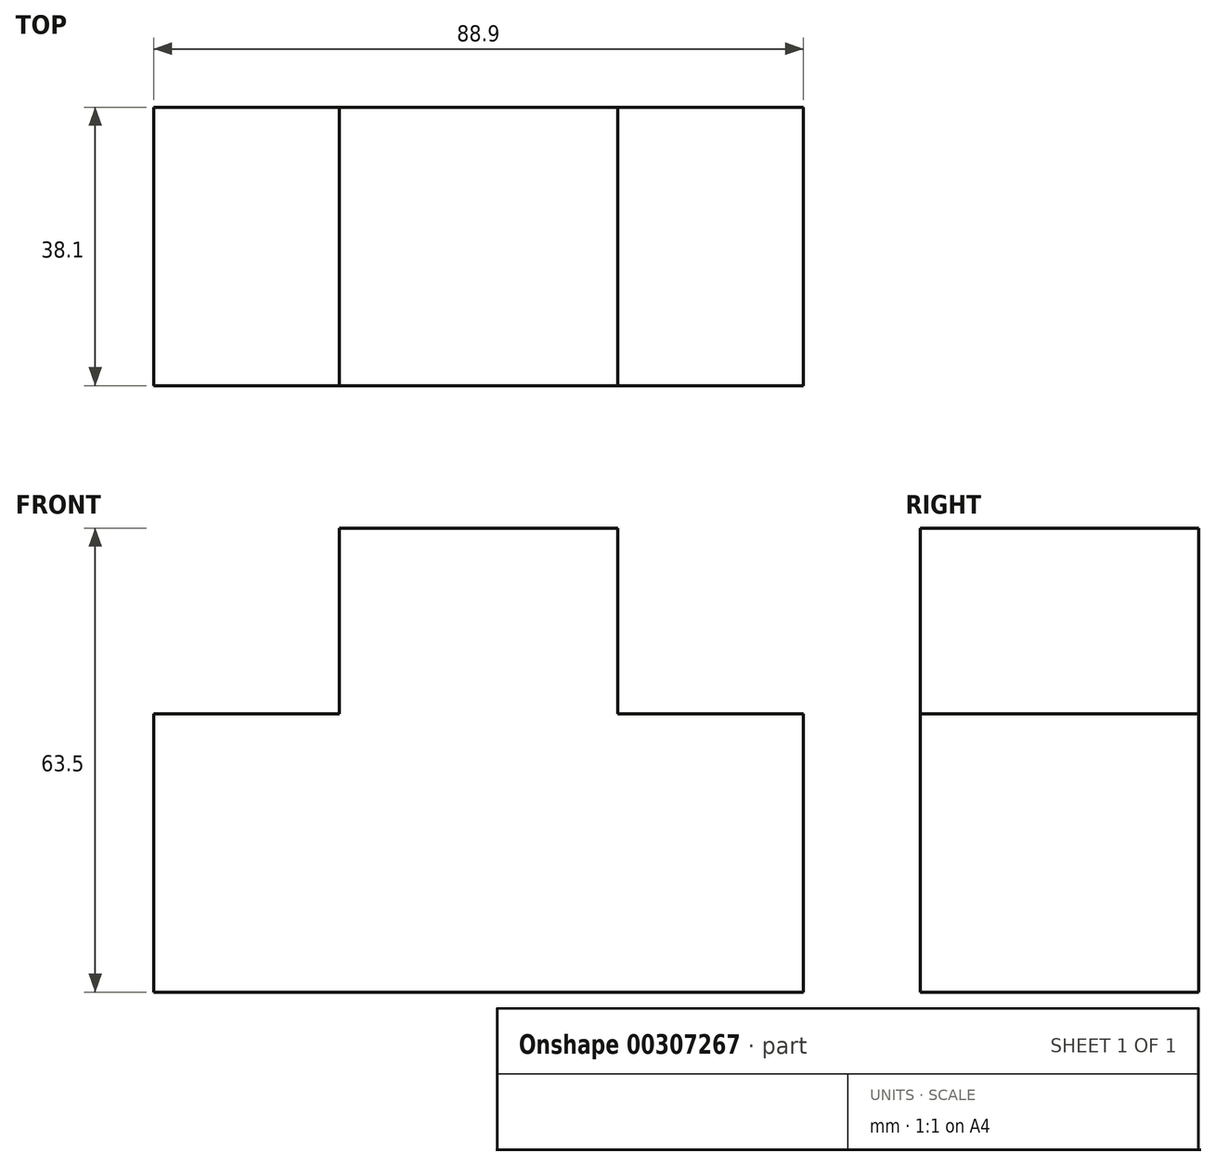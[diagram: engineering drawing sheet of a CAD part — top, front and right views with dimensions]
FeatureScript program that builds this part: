
annotation { "Feature Type Name" : "Feature", "Feature Type Description" : "" }
export const myFeature = defineFeature(function(context is Context, id is Id, definition is map)
    precondition{}
    {
        {
            var Q0;
            Q0=qCreatedBy(makeId("Front.planeOp"),FACE);
            var sketch = newSketch(context, id + "F0", { "sketchPlane" : qUnion([Q0])});
            skLineSegment(sketch, "E0", {"start": v(-40.12, -50.13) * mm, "end": v(48.78, -50.13) * mm});
            skLineSegment(sketch, "E1", {"start": v(48.78, -50.13) * mm, "end": v(48.78, -12.03) * mm});
            skLineSegment(sketch, "E2", {"start": v(48.78, -12.03) * mm, "end": v(23.38, -12.03) * mm});
            skLineSegment(sketch, "E3", {"start": v(23.38, -12.03) * mm, "end": v(23.38, 13.37) * mm});
            skLineSegment(sketch, "E4", {"start": v(23.38, 13.37) * mm, "end": v(-14.72, 13.37) * mm});
            skLineSegment(sketch, "E5", {"start": v(-14.72, 13.37) * mm, "end": v(-14.72, -12.03) * mm});
            skLineSegment(sketch, "E6", {"start": v(-14.72, -12.03) * mm, "end": v(-40.12, -12.03) * mm});
            skLineSegment(sketch, "E7", {"start": v(-40.12, -12.03) * mm, "end": v(-40.12, -50.13) * mm});
            skSolve(sketch);
        }
        {
            var Q0;
            Q0=makeQuery(id+"F0.imprint","IMPRINT",FACE,{"disambiguationData":[TD([[makeQuery(id+"F0.imprint","IMPRINT",EDGE,{"derivedFrom":sQuery(id+"F0.wireOp",EDGE,"E0")}),1.0]])]});
            extrude(context, id + "F1", {"entities" : qUnion([Q0]), "depth" : 38.1 * mm});
        }
    });
